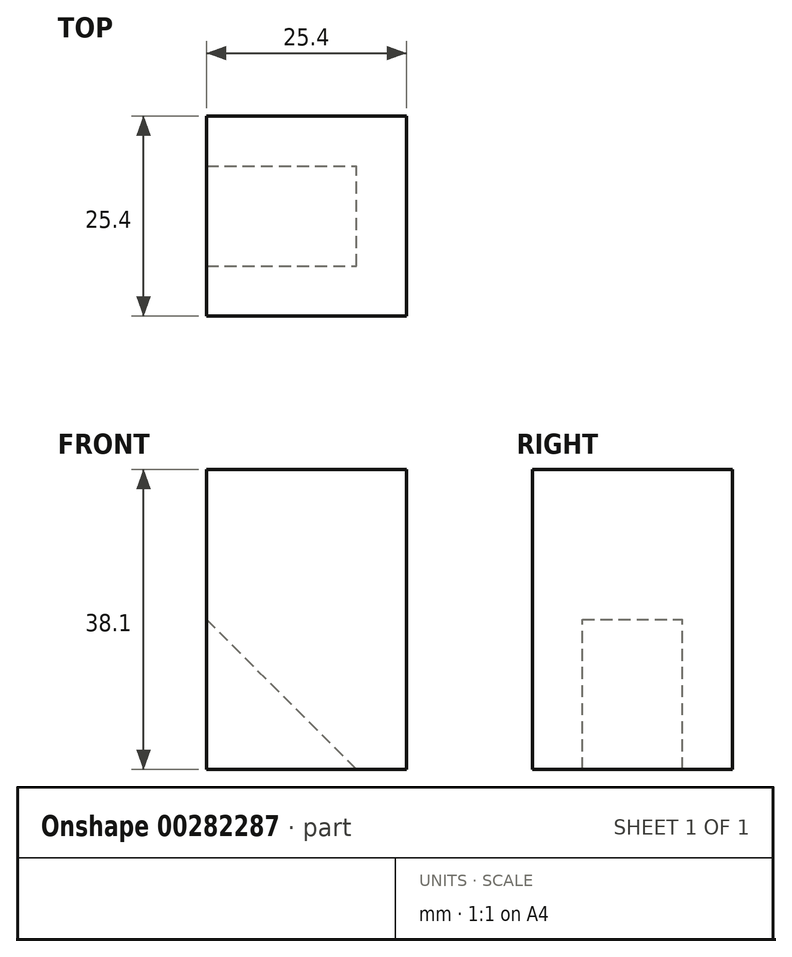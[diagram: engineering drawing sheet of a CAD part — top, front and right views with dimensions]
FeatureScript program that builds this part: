
annotation { "Feature Type Name" : "Feature", "Feature Type Description" : "" }
export const myFeature = defineFeature(function(context is Context, id is Id, definition is map)
    precondition{}
    {
        {
            var Q0;
            Q0=qCreatedBy(makeId("Front.planeOp"),FACE);
            var sketch = newSketch(context, id + "F0", { "sketchPlane" : qUnion([Q0])});
            skLineSegment(sketch, "E0", {"start": v(0, 0) * mm, "end": v(-25.4, 0) * mm});
            skLineSegment(sketch, "E1", {"start": v(-25.4, 0) * mm, "end": v(-25.4, -19.05) * mm});
            skLineSegment(sketch, "E2", {"start": v(-25.4, -19.05) * mm, "end": v(-6.35, -38.1) * mm});
            skLineSegment(sketch, "E3", {"start": v(-6.35, -38.1) * mm, "end": v(0, -38.1) * mm});
            skLineSegment(sketch, "E4", {"start": v(0, -38.1) * mm, "end": v(0, 0) * mm});
            skSolve(sketch);
        }
        {
            var Q0;
            Q0 = qSketchRegion(id + "F0", true);
            extrude(context, id + "F1", {"entities" : qUnion([Q0]), "depth" : 12.7 * mm});
        }
        {
            var Q0;
            Q0=makeQuery(id+"F1.opExtrude","SWEPT_FACE",FACE,{"disambiguationData":[OSD([sQuery(id+"F0.wireOp",EDGE,"E4")])]});
            var sketch = newSketch(context, id + "F2", { "sketchPlane" : qUnion([Q0])});
            skLineSegment(sketch, "E5.bottom", {"start": v(0, -19.05) * mm, "end": v(-12.7, -19.05) * mm});
            skLineSegment(sketch, "E5.top", {"start": v(0, 0) * mm, "end": v(-12.7, 0) * mm});
            skLineSegment(sketch, "E5.left", {"start": v(0, -19.05) * mm, "end": v(0, 0) * mm});
            skLineSegment(sketch, "E5.right", {"start": v(-12.7, -19.05) * mm, "end": v(-12.7, 0) * mm});
            skPoint(sketch, "E6.oppositeSnap0", {"position": v(-6.35, 0) * mm});
            skLineSegment(sketch, "E6.bottom", {"start": v(0, -38.1) * mm, "end": v(6.35, -38.1) * mm});
            skLineSegment(sketch, "E6.top", {"start": v(0, 0) * mm, "end": v(6.35, 0) * mm});
            skLineSegment(sketch, "E6.left", {"start": v(0, -38.1) * mm, "end": v(0, 0) * mm});
            skLineSegment(sketch, "E6.right", {"start": v(6.35, -38.1) * mm, "end": v(6.35, 0) * mm});
            skPoint(sketch, "E7.oppositeSnap0", {"position": v(3.17, 0) * mm});
            skLineSegment(sketch, "E7.bottom", {"start": v(-12.7, -38.1) * mm, "end": v(-19.05, -38.1) * mm});
            skLineSegment(sketch, "E7.top", {"start": v(-12.7, 0) * mm, "end": v(-19.05, 0) * mm});
            skLineSegment(sketch, "E7.left", {"start": v(-12.7, -38.1) * mm, "end": v(-12.7, 0) * mm});
            skLineSegment(sketch, "E7.right", {"start": v(-19.05, -38.1) * mm, "end": v(-19.05, 0) * mm});
            skSolve(sketch);
        }
        {
            var Q0;
            Q0 = qSketchRegion(id + "F2", true);
            extrude(context, id + "F3", {"entities" : qUnion([Q0]), "operationType" : NewBodyOperationType.ADD, "oppositeDirection" : true, "depth" : 25.4 * mm});
        }
    });
